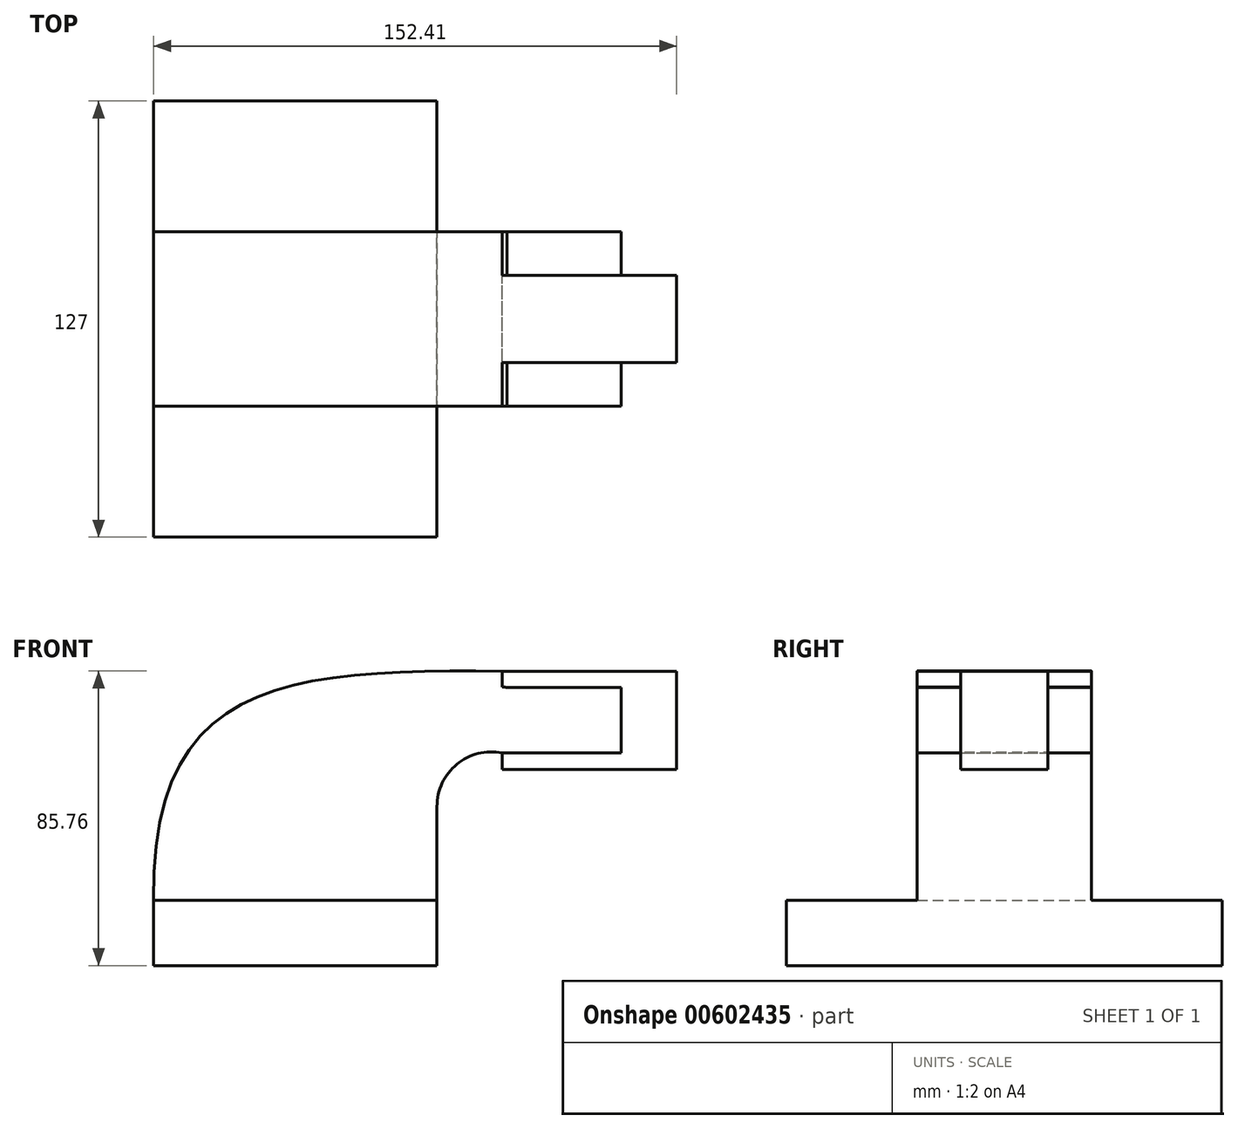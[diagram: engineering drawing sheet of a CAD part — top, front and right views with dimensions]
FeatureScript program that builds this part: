
annotation { "Feature Type Name" : "Feature", "Feature Type Description" : "" }
export const myFeature = defineFeature(function(context is Context, id is Id, definition is map)
    precondition{}
    {
        {
            var Q0;
            Q0=qCreatedBy(makeId("Front.planeOp"),FACE);
            var sketch = newSketch(context, id + "F0", { "sketchPlane" : qUnion([Q0])});
            skLineSegment(sketch, "E0.bottom", {"start": v(-41.28, 9.52) * mm, "end": v(41.28, 9.53) * mm});
            skLineSegment(sketch, "E0.top", {"start": v(-41.28, -9.53) * mm, "end": v(41.28, -9.53) * mm});
            skLineSegment(sketch, "E0.left", {"start": v(-41.28, 9.52) * mm, "end": v(-41.28, -9.53) * mm});
            skLineSegment(sketch, "E0.right", {"start": v(41.28, 9.53) * mm, "end": v(41.28, -9.52) * mm});
            skPoint(sketch, "E0.middle", {"position": v(0, 0) * mm});
            skLineSegment(sketch, "E1.bottom", {"start": v(60.33, 76.2) * mm, "end": v(111.13, 76.2) * mm});
            skLineSegment(sketch, "E1.top", {"start": v(60.33, 47.62) * mm, "end": v(111.12, 47.62) * mm});
            skLineSegment(sketch, "E1.left", {"start": v(60.33, 76.2) * mm, "end": v(60.33, 47.62) * mm});
            skLineSegment(sketch, "E1.right", {"start": v(111.13, 76.2) * mm, "end": v(111.13, 47.62) * mm});
            skPoint(sketch, "E1.middle", {"position": v(85.72, 61.91) * mm});
            skLineSegment(sketch, "E2", {"start": v(41.27, 9.53) * mm, "end": v(41.27, 36.83) * mm});
            skArc(sketch, "E3", {"start": v(41.27, 36.83) * mm, "mid": v(47.07, 49.09) * mm, "end": v(60.22, 52.4) * mm});
            skLineSegment(sketch, "E4", {"start": v(60.22, 52.4) * mm, "end": v(95, 52.4) * mm});
            skLineSegment(sketch, "E5.0", {"start": v(61.72, 71.45) * mm, "end": v(95, 71.45) * mm});
            skArc(sketch, "E5.1", {"start": v(22.22, 36.83) * mm, "mid": v(34.13, 63.09) * mm, "end": v(61.72, 71.45) * mm});
            skLineSegment(sketch, "E5.2", {"start": v(22.22, 9.53) * mm, "end": v(22.22, 36.83) * mm});
            skLineSegment(sketch, "E6", {"start": v(95, 71.45) * mm, "end": v(95, 52.4) * mm});
            skFitSpline(sketch, "E7", {"points": [v(-41.28, 9.52) * mm, v(60.33, 76.2) * mm], "startDerivative": vector(-3.18, 196.78) * mm, "endDerivative": vector(180.98, -1.08) * mm});
            skSolve(sketch);
        }
        {
            var Q0;
            Q0=makeQuery(id+"F0.imprint","IMPRINT",FACE,{"disambiguationData":[TD([[makeQuery(id+"F0.imprint","IMPRINT",EDGE,{"derivedFrom":sQuery(id+"F0.wireOp",EDGE,"E0.top")}),1.0]])]});
            extrude(context, id + "F1", {"entities" : qUnion([Q0]), "endBound" : BoundingType.SYMMETRIC, "oppositeDirection" : true, "depth" : 127 * mm, "offsetDistance" : 25.4 * mm});
        }
        {
            var Q0;
            {var subQ1=sQuery(id+"F0.wireOp",EDGE,"E2");Q0=makeQuery(id+"F0.imprint","IMPRINT",FACE,{"disambiguationData":[TD([[makeQuery(id+"F0.imprint","IMPRINT",EDGE,{"derivedFrom":subQ1}),1.0]])]});}
            extrude(context, id + "F2", {"entities" : qUnion([Q0]), "operationType" : NewBodyOperationType.ADD, "endBound" : BoundingType.SYMMETRIC, "depth" : 50.8 * mm, "offsetDistance" : 25.4 * mm});
        }
        {
            var Q0;
            {var subQ1=sQuery(id+"F0.wireOp",EDGE,"E5.0");Q0=makeQuery(id+"F0.imprint","IMPRINT",FACE,{"disambiguationData":[TD([[makeQuery(id+"F0.imprint","IMPRINT",EDGE,{"derivedFrom":subQ1}),-1.0]])]});}
            extrude(context, id + "F3", {"entities" : qUnion([Q0]), "operationType" : NewBodyOperationType.ADD, "endBound" : BoundingType.SYMMETRIC, "depth" : 50.8 * mm, "offsetDistance" : 25.4 * mm});
        }
        {
            var Q0;
            {var subQ0=sQuery(id+"F0.wireOp",EDGE,"E5.2");Q0=makeQuery(id+"F0.imprint","IMPRINT",FACE,{"disambiguationData":[TD([[makeQuery(id+"F0.imprint","IMPRINT",EDGE,{"derivedFrom":subQ0}),1.0]])]});}
            extrude(context, id + "F4", {"entities" : qUnion([Q0]), "operationType" : NewBodyOperationType.ADD, "endBound" : BoundingType.SYMMETRIC, "depth" : 50.8 * mm, "offsetDistance" : 25.4 * mm});
        }
        {
            var Q0;
            {var subQ4=sQuery(id+"F0.wireOp",EDGE,"E1.bottom");Q0=makeQuery(id+"F0.imprint","IMPRINT",FACE,{"disambiguationData":[TD([[makeQuery(id+"F0.imprint","IMPRINT",EDGE,{"derivedFrom":subQ4}),-1.0]])]});}
            extrude(context, id + "F5", {"entities" : qUnion([Q0]), "operationType" : NewBodyOperationType.ADD, "endBound" : BoundingType.SYMMETRIC, "depth" : 25.4 * mm, "offsetDistance" : 25.4 * mm});
        }
    });
